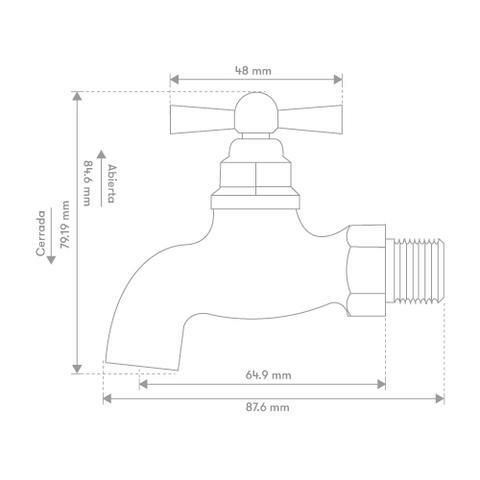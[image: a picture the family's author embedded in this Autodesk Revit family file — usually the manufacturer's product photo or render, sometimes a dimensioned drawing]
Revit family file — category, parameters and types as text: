
# Revit family: BIM_01-9983-11
name_source: partatom
category: Aparatos sanitarios
units: mm (PartAtom-declared; Revit-internal decimal feet)

## family parameters
Activar corte en vistas = No
Anfitrión = Cara
Compartido = No
Corte con vacíos al cargar = No
Cota de conector redondo = Usar diámetro
Mantener orientación de anotación = No
Número OmniClass = 23.31.11.00
Punto de cálculo de habitación = No
Tipo de pieza = Normal

## types (1)
- 01-9983-11
    Acometida = Dim 1/2" NPT
    Alto = 46 mm  [stored 0.150919 ft]
    Ancho = 75 mm
    Ancho manija llave = 48 mm  [stored 0.15748 ft]
    Conexiones = Acometida: Rosca macho ½” NPT.
Manguera: Rosca macho ¾”.
    Conexión AC = Sí
    Conexión AF = Sí
    Conexión de residuos = No
    Conexión de ventilación = No
    Consumo aproximado a 25 psi = 3.8
    Date Modified = 16-09-2025
    Descripción = Llave jardin
    Diametro Nominal = 13.9 mm
    Elevación por defecto = 0 mm  [stored 0 ft]
    Fabricante = Gricol
    Garantia Especifica = 20 Años
    Imagen de tipo = LLAVE MANGUERA LIVIANA METAL CROMADA.PNG
    Laton = Laton
    Link Ficha Tecnica = https://infotecnica.gricol.com
    Materiales del producto = Latón, Zamak, ABS, Polipropileno, Caucho
    Metal Laton Cromado = Metal Laton Cromado
    Metal Zamak Cromado = Metal Zamak Cromado
    Modelo = 01-9983-11
    Presión Maxima = 125.00 psi
    Presión Mínima = 20.00 psi
    Presión de Estaiildo = 500.00 psi
    Product Name = Llave Manguera Metálica Cromada
    Referente Normativo = NTC 1644, ASME A112.18.1 / CSA B125.1
    Resistencia a Corrosión = ensayo según NTC 1156
    Salida = Dim 3/4" NH
    Sitio web = https://www.gricol.com
    Temperaturas de trabajo = 5°C a 71°C
    Tipo de Uso = Uso doméstico para agua potable.
    Torque de Conexioón = 61 Nm
    URL = https://www.gricol.com
    Vida Util = 150.000 Ciclos

note: [stored X ft] marks values corroborated as IEEE doubles in the binary element streams (Revit-internal decimal feet)

## geometry (parser evidence)
native form markers: Blend x2, Sweep x7
no freeform markers — native parametric forms only
